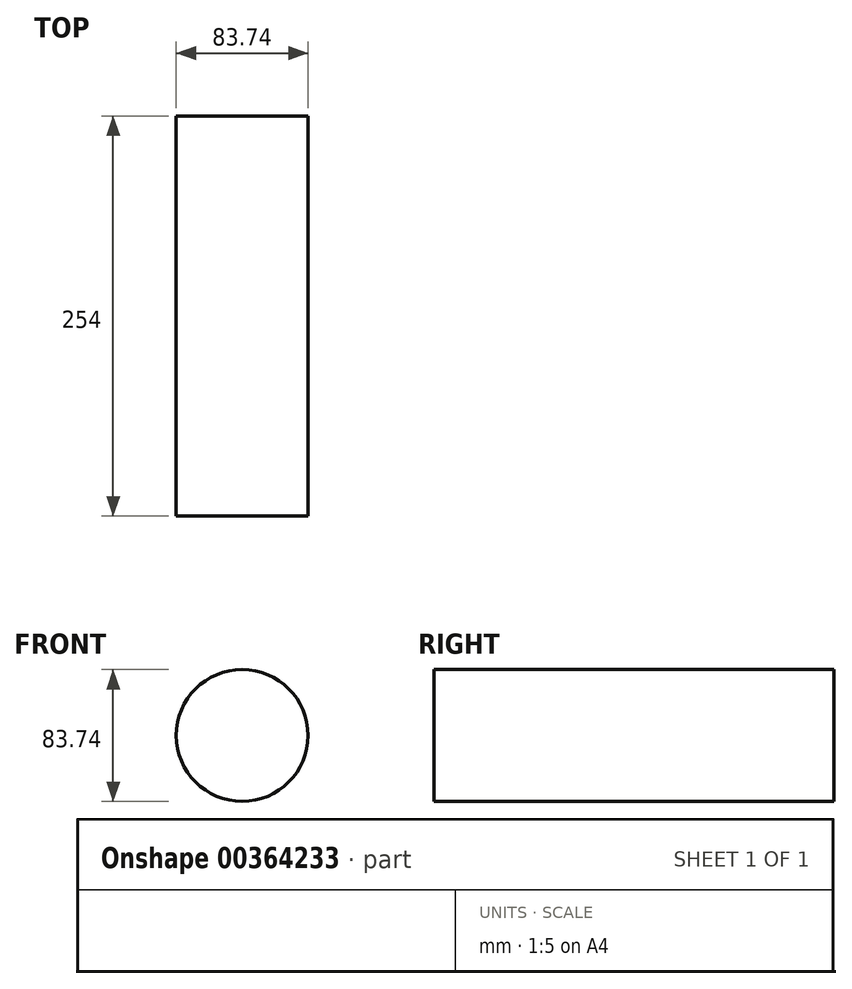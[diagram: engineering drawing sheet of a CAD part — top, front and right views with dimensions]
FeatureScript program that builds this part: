
annotation { "Feature Type Name" : "Feature", "Feature Type Description" : "" }
export const myFeature = defineFeature(function(context is Context, id is Id, definition is map)
    precondition{}
    {
        {
            var Q0;
            Q0=qCreatedBy(makeId("Front.planeOp"),FACE);
            var sketch = newSketch(context, id + "F0", { "sketchPlane" : qUnion([Q0])});
            skCircle(sketch, "E0", {"center": v(0, 0) * mm, "radius": 41.87 * mm});
            skSolve(sketch);
        }
        {
            var Q0;
            Q0 = qSketchRegion(id + "F0", true);
            extrude(context, id + "F1", {"entities" : qUnion([Q0]), "depth" : 254 * mm});
        }
    });
